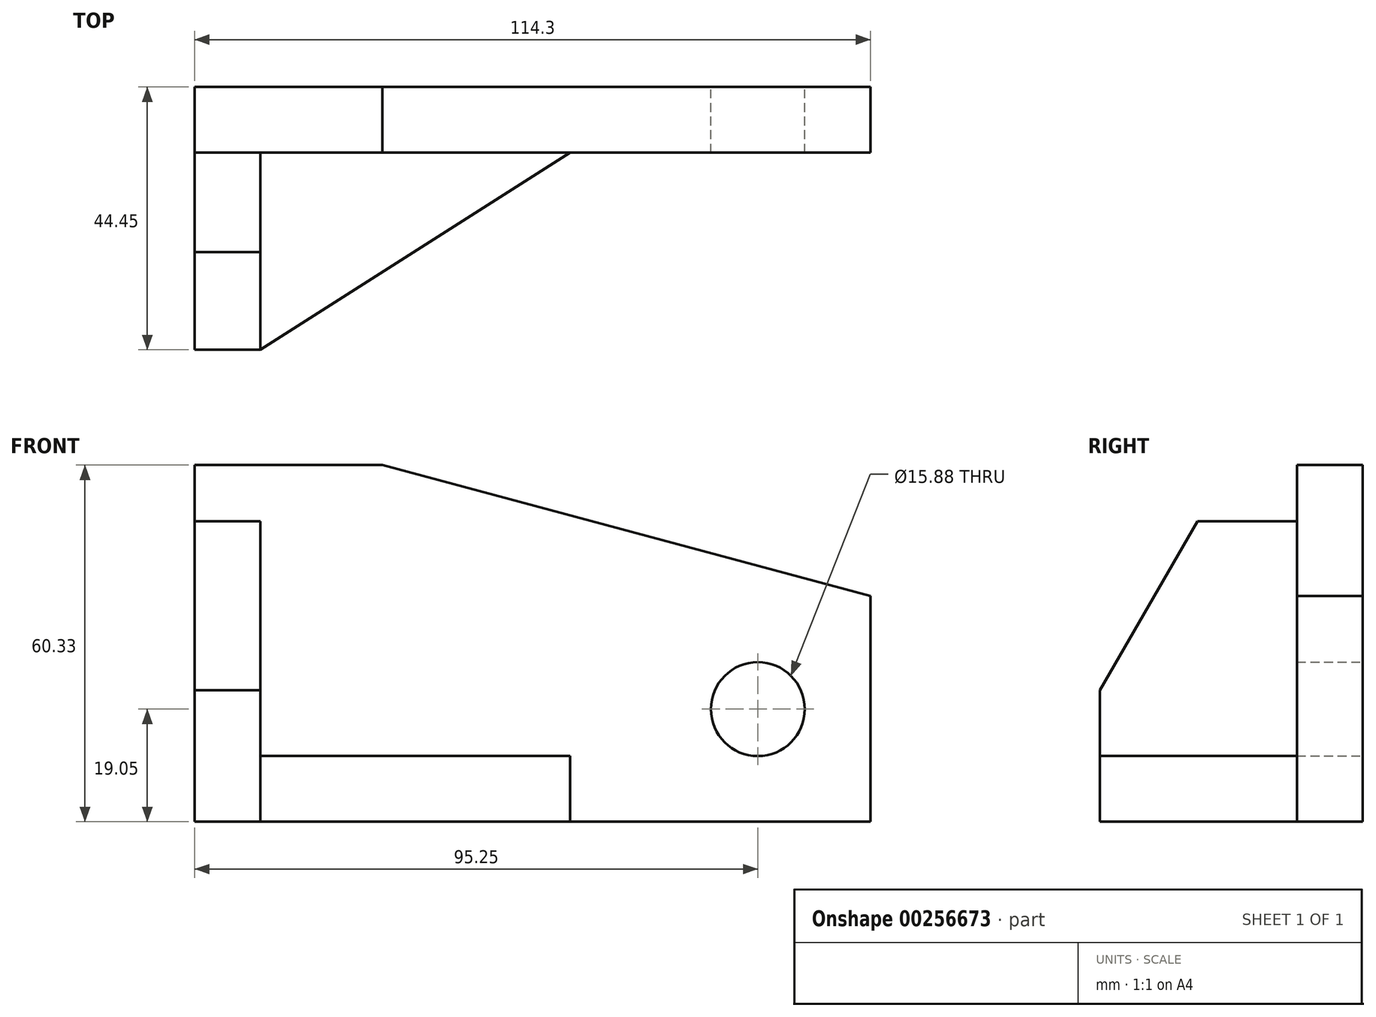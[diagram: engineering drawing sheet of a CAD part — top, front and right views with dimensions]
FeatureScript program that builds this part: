
annotation { "Feature Type Name" : "Feature", "Feature Type Description" : "" }
export const myFeature = defineFeature(function(context is Context, id is Id, definition is map)
    precondition{}
    {
        {
            var Q0;
            Q0=qCreatedBy(makeId("Top.planeOp"),FACE);
            var sketch = newSketch(context, id + "F0", { "sketchPlane" : qUnion([Q0])});
            skLineSegment(sketch, "E0", {"start": v(0, 0) * mm, "end": v(114.3, 0) * mm});
            skLineSegment(sketch, "E1", {"start": v(0, 0) * mm, "end": v(0, -44.45) * mm});
            skLineSegment(sketch, "E2", {"start": v(0, -44.45) * mm, "end": v(11.11, -44.45) * mm});
            skLineSegment(sketch, "E3", {"start": v(114.3, 0) * mm, "end": v(114.3, -11.11) * mm});
            skLineSegment(sketch, "E4", {"start": v(114.3, -11.11) * mm, "end": v(0, -11.11) * mm});
            skLineSegment(sketch, "E5", {"start": v(11.11, -44.45) * mm, "end": v(11.11, -11.11) * mm});
            skPoint(sketch, "E6.endSnap0", {"position": v(5.56, -44.45) * mm});
            skLineSegment(sketch, "E7", {"start": v(63.5, -11.11) * mm, "end": v(11.11, -44.45) * mm});
            skSolve(sketch);
        }
        {
            var Q0;
            {var subQ4=sQuery(id+"F0.wireOp",EDGE,"E0");Q0=makeQuery(id+"F0.imprint","IMPRINT",FACE,{"disambiguationData":[TD([[makeQuery(id+"F0.imprint","IMPRINT",EDGE,{"derivedFrom":subQ4}),-1.0]])]});}
            extrude(context, id + "F1", {"entities" : qUnion([Q0]), "depth" : 60.32 * mm});
        }
        {
            var Q0;
            {var subQ4=sQuery(id+"F0.wireOp",EDGE,"E5");Q0=makeQuery(id+"F0.imprint","IMPRINT",FACE,{"disambiguationData":[TD([[makeQuery(id+"F0.imprint","IMPRINT",EDGE,{"derivedFrom":subQ4}),1.0]])]});}
            extrude(context, id + "F2", {"entities" : qUnion([Q0]), "operationType" : NewBodyOperationType.ADD, "depth" : 50.8 * mm});
        }
        {
            var Q0;
            {var subQ0=sQuery(id+"F0.wireOp",EDGE,"E5");Q0=makeQuery(id+"F0.imprint","IMPRINT",FACE,{"disambiguationData":[TD([[makeQuery(id+"F0.imprint","IMPRINT",EDGE,{"derivedFrom":subQ0}),-1.0]])]});}
            extrude(context, id + "F3", {"entities" : qUnion([Q0]), "operationType" : NewBodyOperationType.ADD, "depth" : 11.1 * mm});
        }
        {
            var Q0;
            {var subQ0=sQuery(id+"F0.wireOp",EDGE,"E1");Q0=makeQuery(id+"F2.boolean.opBoolean","MERGE",FACE,{"derivedFrom":[makeQuery(id+"F1.opExtrude","SWEPT_FACE",FACE,{"disambiguationData":[OSD([subQ0])]}),makeQuery(id+"F2.opExtrude","SWEPT_FACE",FACE,{"disambiguationData":[OSD([subQ0])]})]});}
            var sketch = newSketch(context, id + "F4", { "sketchPlane" : qUnion([Q0])});
            skLineSegment(sketch, "E8", {"start": v(44.45, 0) * mm, "end": v(44.45, 22.23) * mm});
            skLineSegment(sketch, "E9", {"start": v(44.45, 22.23) * mm, "end": v(27.95, 50.8) * mm});
            skSolve(sketch);
        }
        {
            var Q0;
            {var subQ0=sQuery(id+"F4.wireOp",EDGE,"E9");Q0=makeQuery(id+"F4.imprint","IMPRINT",FACE,{"disambiguationData":[TD([[makeQuery(id+"F4.imprint","IMPRINT",EDGE,{"derivedFrom":subQ0}),-1.0]])]});}
            extrude(context, id + "F5", {"entities" : qUnion([Q0]), "operationType" : NewBodyOperationType.REMOVE, "endBound" : BoundingType.UP_TO_NEXT, "oppositeDirection" : true, "depth" : 25.4 * mm});
        }
        {
            var Q0;
            Q0=makeQuery(id+"F1.opExtrude","SWEPT_FACE",FACE,{"disambiguationData":[OSD([sQuery(id+"F0.wireOp",EDGE,"E0")])]});
            var sketch = newSketch(context, id + "F6", { "sketchPlane" : qUnion([Q0])});
            skLineSegment(sketch, "E10", {"start": v(0, 60.33) * mm, "end": v(-31.75, 60.33) * mm});
            skLineSegment(sketch, "E11", {"start": v(-31.75, 60.33) * mm, "end": v(-114.3, 38.2) * mm});
            skLineSegment(sketch, "E12", {"start": v(-114.3, 0) * mm, "end": v(-95.25, 0) * mm});
            skLineSegment(sketch, "E13", {"start": v(-95.25, 0) * mm, "end": v(-95.25, 11.11) * mm});
            skCircle(sketch, "E14", {"center": v(-95.25, 19.05) * mm, "radius": 7.94 * mm});
            skSolve(sketch);
        }
        {
            var Q0;
            Q0=makeQuery(id+"F6.imprint","IMPRINT",FACE,{"disambiguationData":[TD([[makeQuery(id+"F6.imprint","IMPRINT",EDGE,{"derivedFrom":sQuery(id+"F6.wireOp",EDGE,"E14")}),1.0]])]});
            var Q1;
            {var subQ0=sQuery(id+"F6.wireOp",EDGE,"E11");Q1=makeQuery(id+"F6.imprint","IMPRINT",FACE,{"disambiguationData":[TD([[makeQuery(id+"F6.imprint","IMPRINT",EDGE,{"derivedFrom":subQ0}),-1.0]])]});}
            extrude(context, id + "F7", {"entities" : qUnion([Q0, Q1]), "operationType" : NewBodyOperationType.REMOVE, "endBound" : BoundingType.UP_TO_NEXT, "oppositeDirection" : true, "depth" : 25.4 * mm});
        }
    });
